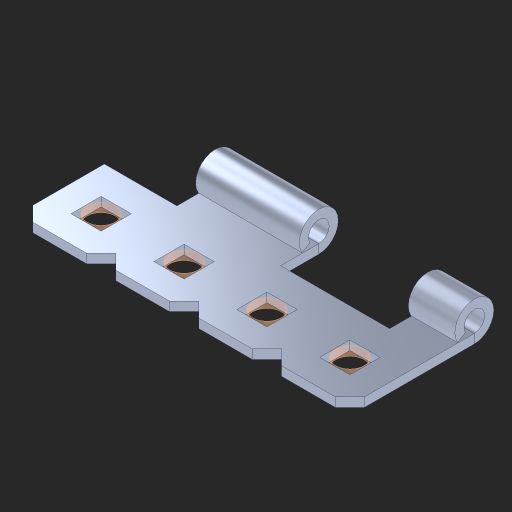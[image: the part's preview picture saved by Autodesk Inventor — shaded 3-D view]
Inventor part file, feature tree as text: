
AUTODESK INVENTOR PART (.ipt)
format: ipt  version: 2023 (Build 270158000, 158)  size: 204,800 bytes
history: native  units: in
note: dims shown in document units (in); Inventor stores cm internally (conversion verified against a paired STEP export)
features: other x6, extrude x5, sketch x2, pattern_linear x1, imported_body x1
ambient origin geometry x8: Origin, YZ Plane, XZ Plane, XY Plane, X Axis, Y Axis, Z Axis, Center Point
bodies: Body1 (feature_tree), Body2 (feature_tree), Body3 (feature_tree), Body4 (feature_tree), Body5 (feature_tree)
feature tree (15):
  other  "Cut-Extrude3"
  other  "Top"
  pattern_linear  "Rectangular Pattern2"  Spacing1=0.5in  [1 undecoded]
  extrude  "Extrusion1"  Depth=0.5in
  imported_body  "Base1"
  sketch  "Sketch4"  dims[d30=0.172in]
  other  "Srf6"
  other  "Srf7"
  other  "Srf8"
  other  "Srf9"
  sketch  "Sketch5"  dims[d31=0.055in d32=0.0in d35=0.5in d36=0.5in d37=0.0in]
  extrude  "ExtrusionSrf6"  TaperAngle=0.0deg  [1 undecoded]
  extrude  "ExtrusionSrf7"  [1 undecoded]
  extrude  "ExtrusionSrf8"  [1 undecoded]
  extrude  "ExtrusionSrf9"  [1 undecoded]
note: 5 required parameter values undecoded (feature->parameter linkage not recoverable at this tier; creation-order binding heuristic only, values carry confidence <= 0.55)
